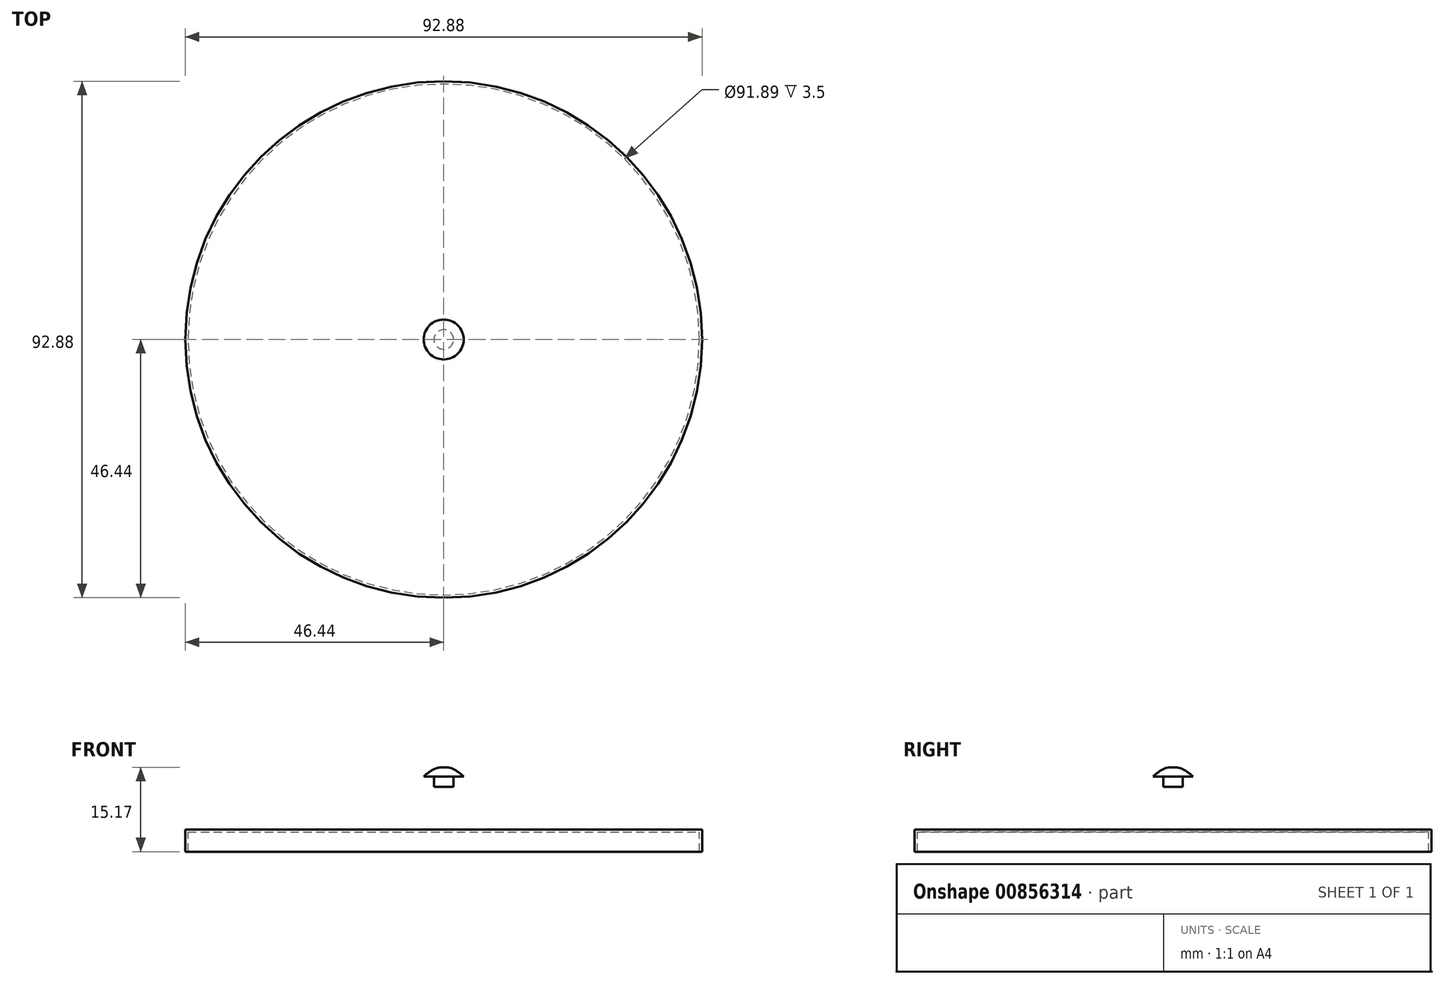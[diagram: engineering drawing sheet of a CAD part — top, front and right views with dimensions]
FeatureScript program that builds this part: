
annotation { "Feature Type Name" : "Feature", "Feature Type Description" : "" }
export const myFeature = defineFeature(function(context is Context, id is Id, definition is map)
    precondition{}
    {
        {
            var Q0;
            Q0=qCreatedBy(makeId("Front.planeOp"),FACE);
            var sketch = newSketch(context, id + "F0", { "sketchPlane" : qUnion([Q0])});
            skLineSegment(sketch, "E0", {"start": v(-46.44, 0) * mm, "end": v(48.56, 0) * mm});
            skLineSegment(sketch, "E1", {"start": v(-46.44, 0) * mm, "end": v(-46.44, 4) * mm});
            skLineSegment(sketch, "E2", {"start": v(-46.44, 4) * mm, "end": v(-48.94, 4) * mm});
            skFitSpline(sketch, "E3", {"points": [v(-48.94, 4) * mm, v(0, 11.67) * mm, v(51.06, 4) * mm], "startDerivative": vector(98.3, 23.07) * mm, "endDerivative": vector(101.08, -22.93) * mm});
            skLineSegment(sketch, "E4", {"start": v(-48.94, 4) * mm, "end": v(51.06, 4) * mm});
            skLineSegment(sketch, "E5", {"start": v(48.56, 0) * mm, "end": v(48.56, 4) * mm});
            skLineSegment(sketch, "E6", {"start": v(-1.76, 11.65) * mm, "end": v(-1.76, 13.53) * mm});
            skLineSegment(sketch, "E7", {"start": v(-1.76, 13.53) * mm, "end": v(-3.58, 13.53) * mm});
            skFitSpline(sketch, "E8", {"points": [v(-3.58, 13.53) * mm, v(0, 15.15) * mm, v(3.47, 13.53) * mm, v(1.9, 13.53) * mm], "startDerivative": vector(8.13, 6.93) * mm, "endDerivative": vector(-9.81, 1.36) * mm});
            skLineSegment(sketch, "E9", {"start": v(1.9, 13.53) * mm, "end": v(1.9, 11.67) * mm});
            skLineSegment(sketch, "E10", {"start": v(0, 43.53) * mm, "end": v(0, -37.04) * mm});
            skSolve(sketch);
        }
        {
            var Q0;
            {var subQ4=sQuery(id+"F0.wireOp",EDGE,"E6");Q0=makeQuery(id+"F0.imprint","IMPRINT",FACE,{"disambiguationData":[TD([[makeQuery(id+"F0.imprint","IMPRINT",EDGE,{"derivedFrom":subQ4}),-1.0]])]});}
            var Q1;
            {var subQ0=sQuery(id+"F0.wireOp",EDGE,"E4");var subQ4=sQuery(id+"F0.wireOp",EDGE,"E3");var subQ5=makeQuery(id+"F0.imprint","INTERSECT",VERTEX,{"disambiguationData":[OD(0.0)],"derivedFrom":[subQ4,subQ0]});Q1=makeQuery(id+"F0.imprint","IMPRINT",FACE,{"disambiguationData":[TD([[makeQuery(id+"F0.imprint","IMPRINT",EDGE,{"disambiguationData":[TD([[subQ5,-1.0]])],"derivedFrom":subQ4}),-1.0]])]});}
            var Q2;
            {var subQ0=sQuery(id+"F0.wireOp",EDGE,"E1");Q2=makeQuery(id+"F0.imprint","IMPRINT",FACE,{"disambiguationData":[TD([[makeQuery(id+"F0.imprint","IMPRINT",EDGE,{"derivedFrom":subQ0}),-1.0]])]});}
            var Q3;
            Q3=sQuery(id+"F0.wireOp",EDGE,"E10");
            revolve(context, id + "F1", {"surfaceOperationType" : NewSurfaceOperationType.NEW, "entities" : qUnion([Q0, Q1, Q2]), "axis" : qUnion([Q3]), "revolveType" : RevolveType.FULL});
        }
        {
            var Q0;
            Q0=makeQuery(id+"F1.opRevolve","SWEPT_FACE",FACE,{"disambiguationData":[OSD([sQuery(id+"F0.wireOp",EDGE,"E0")])]});
            shell(context, id + "F2", {"entities" : qUnion([Q0]), "thickness" : 0.5 * mm});
        }
    });
